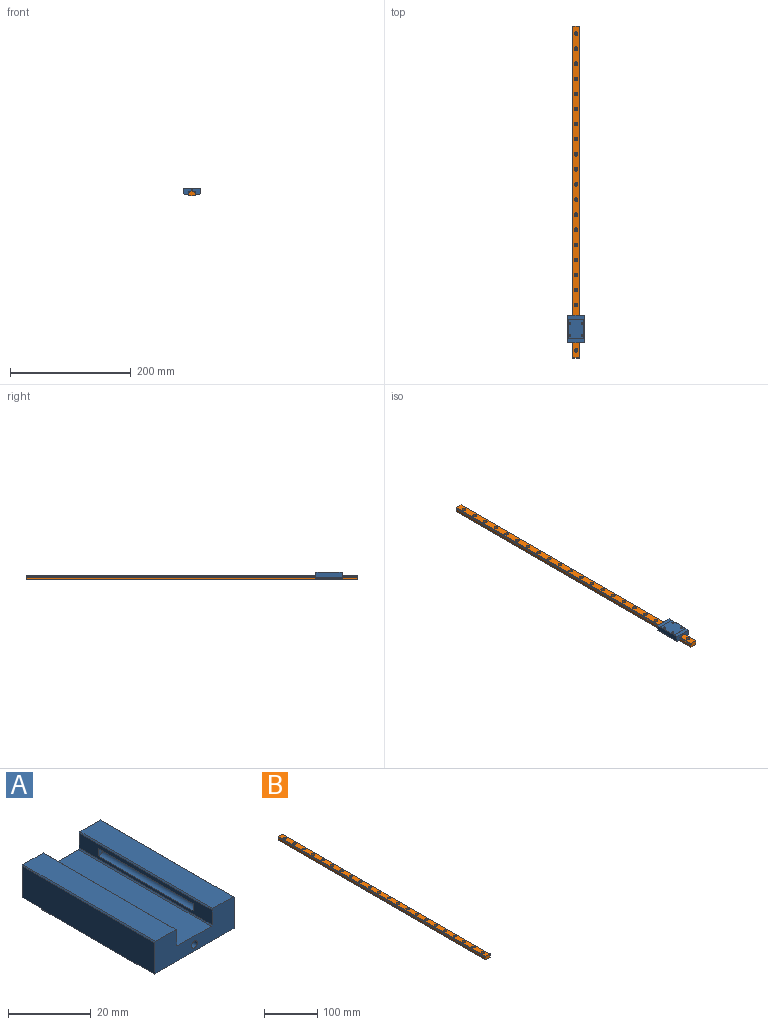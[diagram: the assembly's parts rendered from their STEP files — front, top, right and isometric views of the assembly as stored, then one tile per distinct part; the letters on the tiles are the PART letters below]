
ASSEMBLY  parts=2 mates=1
PART A: 37 faces, bbox 27x45.4x10 mm
  f0: plane 45.4x0.3mm, normal (-0.71,0,0.71), area 19.3mm2, adj f3,f6,f22,f23
  f1: plane 45.4x0.3mm, normal (0.71,0,0.71), area 19.3mm2, adj f10,f11,f22,f23
  f2: plane 45.4x0.3mm, normal (0.71,0,0.71), area 19.3mm2, adj f6,f7,f22,f23
  f3: plane 45.4x4.4mm, normal (-1,0,0), area 129.2mm2, adj f0,f5,f17,f20,f22,f23,f24
  f4: plane 45.4x11.4mm, normal (0,0,1), area 517.6mm2, adj f16,f17,f22,f23
  f5: cylinder r=1.15mm len=32.4mm, axis (0,-1,0), area 141.5mm2, adj f3,f20,f24
  f6: plane 45.4x6.9mm, normal (0,0,1), area 313.3mm2, adj f0,f2,f22,f23
  f7: plane 45.4x9.4mm, normal (1,0,0), area 424.2mm2, adj f2,f15,f18,f21,f22,f23,f25,f35
  f8: plane 32.4x26.4mm, normal (0,0,-1), area 821.1mm2, adj f14,f15,f18,f27,f29,f31,f33,f35
  f9: plane 45.4x9.4mm, normal (-1,0,0), area 424.2mm2, adj f14,f18,f21,f22,f23,f25,f34,f35
  f10: plane 45.4x6.9mm, normal (0,0,1), area 313.3mm2, adj f1,f22,f23,f34
  f11: plane 45.4x4.4mm, normal (1,0,0), area 129.2mm2, adj f1,f12,f16,f19,f22,f23,f36
  f12: cylinder r=1.15mm len=32.4mm, axis (0,-1,0), area 141.5mm2, adj f11,f19,f36
  f13: cylinder r=1mm len=45.4mm, axis (0,-1,0), area 285.3mm2, adj f22,f23
  f14: plane 32.4x0.3mm, normal (-0.71,0,-0.71), area 13.7mm2, adj f8,f9,f18,f35
  f15: plane 32.4x0.3mm, normal (0.71,0,-0.71), area 13.7mm2, adj f7,f8,f18,f35
  f16: plane 45.4x0.3mm, normal (0.71,0,0.71), area 19.3mm2, adj f4,f11,f22,f23
  f17: plane 45.4x0.3mm, normal (-0.71,0,0.71), area 19.3mm2, adj f3,f4,f22,f23
  f18: plane 27x0.5mm, normal (0,-1,0), area 13.4mm2, adj f7,f8,f9,f14,f15,f21
  f19: plane 2.3x1.52mm, normal (0,1,0), area 2.9mm2, adj f11,f12
  f20: plane 2.3x1.52mm, normal (0,1,0), area 2.9mm2, adj f3,f5
  f21: plane 27x6.5mm, normal (0,0,-1), area 175.5mm2, adj f7,f9,f18,f22
  f22: plane 27x9.5mm, normal (0,-1,0), area 193.3mm2, adj f0,f1,f2,f3,f4,f6,f7,f9
  f23: plane 27x9.5mm, normal (0,1,0), area 193.3mm2, adj f0,f1,f2,f3,f4,f6,f7,f9
  f24: plane 2.3x1.52mm, normal (0,-1,0), area 2.9mm2, adj f3,f5
  f25: plane 27x6.5mm, normal (0,0,-1), area 175.5mm2, adj f7,f9,f23,f35
  f26: cone r=857.17mm half-angle=59deg, axis (0,0,-1), area 10mm2, adj f27
  f27: cylinder r=1.65mm len=3.5mm, axis (0,0,1), area 36.3mm2, adj f8,f26
  f28: cone r=857.17mm half-angle=59deg, axis (0,0,-1), area 10mm2, adj f29
  f29: cylinder r=1.65mm len=3.5mm, axis (0,0,1), area 36.3mm2, adj f8,f28
  f30: cone r=857.17mm half-angle=59deg, axis (0,0,-1), area 10mm2, adj f31
  f31: cylinder r=1.65mm len=3.5mm, axis (0,0,1), area 36.3mm2, adj f8,f30
  f32: cone r=857.17mm half-angle=59deg, axis (0,0,-1), area 10mm2, adj f33
  f33: cylinder r=1.65mm len=3.5mm, axis (0,0,1), area 36.3mm2, adj f8,f32
  f34: plane 45.4x0.3mm, normal (-0.71,0,0.71), area 19.3mm2, adj f9,f10,f22,f23
  f35: plane 27x0.5mm, normal (0,1,0), area 13.4mm2, adj f7,f8,f9,f14,f15,f25
  f36: plane 2.3x1.52mm, normal (0,-1,0), area 2.9mm2, adj f11,f12
PART B: 88 faces, bbox 12x550x8 mm
  f0: plane 550x0.51mm, normal (0,0,1), area 280.4mm2, adj f1,f19,f20,f84
  f1: plane 550x0.3mm, normal (1,0,0), area 165mm2, adj f0,f2,f20,f84
  f2: plane 550x0.51mm, normal (0,0,-1), area 280.4mm2, adj f1,f3,f20,f84
  f3: cylinder r=1.15mm len=550mm, axis (0,1,0), area 703.6mm2, adj f2,f4,f20,f84
  f4: plane 550x0.86mm, normal (1,0,0), area 473.5mm2, adj f3,f5,f20,f84
  f5: plane 550x0.35mm, normal (0.71,0,0.71), area 272.2mm2, adj f4,f6,f20,f84
  f6: plane 550x11.3mm, normal (0,0,1), area 5593mm2, adj f5,f7,f20,f23,f26,f29,f32,f35
  f7: plane 550x0.35mm, normal (-0.71,0,0.71), area 272.2mm2, adj f6,f8,f20,f84
  f8: plane 550x0.86mm, normal (-1,0,0), area 473.5mm2, adj f7,f9,f20,f84
  f9: cylinder r=1.15mm len=550mm, axis (0,1,0), area 703.6mm2, adj f8,f10,f20,f84
  f10: plane 550x0.51mm, normal (0,0,-1), area 280.4mm2, adj f9,f11,f20,f84
  f11: plane 550x0.3mm, normal (-1,0,0), area 165mm2, adj f10,f12,f20,f84
  f12: plane 550x0.51mm, normal (0,0,1), area 280.4mm2, adj f11,f13,f20,f84
  f13: cylinder r=1.15mm len=550mm, axis (0,1,0), area 703.6mm2, adj f12,f14,f20,f84
  f14: plane 550x4.26mm, normal (-1,0,0), area 2343.7mm2, adj f13,f15,f20,f84
  f15: plane 550x0.35mm, normal (-0.71,0,-0.71), area 272.2mm2, adj f14,f16,f20,f84
  f16: plane 550x11.3mm, normal (0,0,-1), area 6003.3mm2, adj f15,f17,f20,f21,f24,f27,f30,f33
  f17: plane 550x0.35mm, normal (0.71,0,-0.71), area 272.2mm2, adj f16,f18,f20,f84
  f18: plane 550x4.26mm, normal (1,0,0), area 2343.7mm2, adj f17,f19,f20,f84
  f19: cylinder r=1.15mm len=550mm, axis (0,1,0), area 703.6mm2, adj f0,f18,f20,f84
  f20: plane 12x8mm, normal (0,-1,0), area 93mm2, adj f0,f1,f2,f3,f4,f5,f6,f7
  f21: cylinder r=1.75mm len=3.5mm, axis (0,0,1), area 38.5mm2, adj f16,f22
  f22: plane 6x6mm, normal (0,0,1), area 18.7mm2, adj f21,f23
  f23: cylinder r=3mm len=6mm, axis (0,0,1), area 84.8mm2, adj f6,f22
  f24: cylinder r=1.75mm len=3.5mm, axis (0,0,1), area 38.5mm2, adj f16,f25
  f25: plane 6x6mm, normal (0,0,1), area 18.7mm2, adj f24,f26
  f26: cylinder r=3mm len=6mm, axis (0,0,1), area 84.8mm2, adj f6,f25
  f27: cylinder r=1.75mm len=3.5mm, axis (0,0,1), area 38.5mm2, adj f16,f28
  f28: plane 6x6mm, normal (0,0,1), area 18.7mm2, adj f27,f29
  f29: cylinder r=3mm len=6mm, axis (0,0,1), area 84.8mm2, adj f6,f28
  f30: cylinder r=1.75mm len=3.5mm, axis (0,0,1), area 38.5mm2, adj f16,f31
  f31: plane 6x6mm, normal (0,0,1), area 18.7mm2, adj f30,f32
  f32: cylinder r=3mm len=6mm, axis (0,0,1), area 84.8mm2, adj f6,f31
  f33: cylinder r=1.75mm len=3.5mm, axis (0,0,1), area 38.5mm2, adj f16,f34
  f34: plane 6x6mm, normal (0,0,1), area 18.7mm2, adj f33,f35
  f35: cylinder r=3mm len=6mm, axis (0,0,1), area 84.8mm2, adj f6,f34
  f36: cylinder r=1.75mm len=3.5mm, axis (0,0,1), area 38.5mm2, adj f16,f37
  f37: plane 6x6mm, normal (0,0,1), area 18.7mm2, adj f36,f38
  f38: cylinder r=3mm len=6mm, axis (0,0,1), area 84.8mm2, adj f6,f37
  f39: cylinder r=1.75mm len=3.5mm, axis (0,0,1), area 38.5mm2, adj f16,f40
  f40: plane 6x6mm, normal (0,0,1), area 18.7mm2, adj f39,f41
  f41: cylinder r=3mm len=6mm, axis (0,0,1), area 84.8mm2, adj f6,f40
  f42: cylinder r=1.75mm len=3.5mm, axis (0,0,1), area 38.5mm2, adj f16,f43
  f43: plane 6x6mm, normal (0,0,1), area 18.7mm2, adj f42,f44
  f44: cylinder r=3mm len=6mm, axis (0,0,1), area 84.8mm2, adj f6,f43
  f45: cylinder r=1.75mm len=3.5mm, axis (0,0,1), area 38.5mm2, adj f16,f46
  f46: plane 6x6mm, normal (0,0,1), area 18.7mm2, adj f45,f47
  f47: cylinder r=3mm len=6mm, axis (0,0,1), area 84.8mm2, adj f6,f46
  f48: cylinder r=1.75mm len=3.5mm, axis (0,0,1), area 38.5mm2, adj f16,f49
  f49: plane 6x6mm, normal (0,0,1), area 18.7mm2, adj f48,f50
  f50: cylinder r=3mm len=6mm, axis (0,0,1), area 84.8mm2, adj f6,f49
  f51: cylinder r=1.75mm len=3.5mm, axis (0,0,1), area 38.5mm2, adj f16,f52
  f52: plane 6x6mm, normal (0,0,1), area 18.7mm2, adj f51,f53
  f53: cylinder r=3mm len=6mm, axis (0,0,1), area 84.8mm2, adj f6,f52
  f54: cylinder r=1.75mm len=3.5mm, axis (0,0,1), area 38.5mm2, adj f16,f55
  f55: plane 6x6mm, normal (0,0,1), area 18.7mm2, adj f54,f56
  f56: cylinder r=3mm len=6mm, axis (0,0,1), area 84.8mm2, adj f6,f55
  f57: cylinder r=1.75mm len=3.5mm, axis (0,0,1), area 38.5mm2, adj f16,f58
  f58: plane 6x6mm, normal (0,0,1), area 18.7mm2, adj f57,f59
  f59: cylinder r=3mm len=6mm, axis (0,0,1), area 84.8mm2, adj f6,f58
  f60: cylinder r=1.75mm len=3.5mm, axis (0,0,1), area 38.5mm2, adj f16,f61
  f61: plane 6x6mm, normal (0,0,1), area 18.7mm2, adj f60,f62
  f62: cylinder r=3mm len=6mm, axis (0,0,1), area 84.8mm2, adj f6,f61
  f63: cylinder r=1.75mm len=3.5mm, axis (0,0,1), area 38.5mm2, adj f16,f64
  f64: plane 6x6mm, normal (0,0,1), area 18.7mm2, adj f63,f65
  f65: cylinder r=3mm len=6mm, axis (0,0,1), area 84.8mm2, adj f6,f64
  f66: cylinder r=1.75mm len=3.5mm, axis (0,0,1), area 38.5mm2, adj f16,f67
  f67: plane 6x6mm, normal (0,0,1), area 18.7mm2, adj f66,f68
  f68: cylinder r=3mm len=6mm, axis (0,0,1), area 84.8mm2, adj f6,f67
  f69: cylinder r=1.75mm len=3.5mm, axis (0,0,1), area 38.5mm2, adj f16,f70
  f70: plane 6x6mm, normal (0,0,1), area 18.7mm2, adj f69,f71
  f71: cylinder r=3mm len=6mm, axis (0,0,1), area 84.8mm2, adj f6,f70
  f72: cylinder r=1.75mm len=3.5mm, axis (0,0,1), area 38.5mm2, adj f16,f73
  f73: plane 6x6mm, normal (0,0,1), area 18.7mm2, adj f72,f74
  f74: cylinder r=3mm len=6mm, axis (0,0,1), area 84.8mm2, adj f6,f73
  f75: cylinder r=1.75mm len=3.5mm, axis (0,0,1), area 38.5mm2, adj f16,f76
  f76: plane 6x6mm, normal (0,0,1), area 18.7mm2, adj f75,f77
  f77: cylinder r=3mm len=6mm, axis (0,0,1), area 84.8mm2, adj f6,f76
  f78: cylinder r=1.75mm len=3.5mm, axis (0,0,1), area 38.5mm2, adj f16,f79
  f79: plane 6x6mm, normal (0,0,1), area 18.7mm2, adj f78,f80
  f80: cylinder r=3mm len=6mm, axis (0,0,1), area 84.8mm2, adj f6,f79
  f81: cylinder r=1.75mm len=3.5mm, axis (0,0,1), area 38.5mm2, adj f16,f82
  f82: plane 6x6mm, normal (0,0,1), area 18.7mm2, adj f81,f83
  f83: cylinder r=3mm len=6mm, axis (0,0,1), area 84.8mm2, adj f6,f82
  f84: plane 12x8mm, normal (0,1,0), area 93mm2, adj f0,f1,f2,f3,f4,f5,f6,f7
  f85: cylinder r=1.75mm len=3.5mm, axis (0,0,1), area 38.5mm2, adj f16,f86
  f86: plane 6x6mm, normal (0,0,1), area 18.7mm2, adj f85,f87
  f87: cylinder r=3mm len=6mm, axis (0,0,1), area 84.8mm2, adj f6,f86
PLACE A rot(axis=(0,1,0),180deg) t=(-12.45,82.04,13.68)mm
PLACE B t=(-12.45,43,13.68)mm fixed
MATE slider B.f20 <-> A.f22  axis (0,-1,0) through (-12.45,18,13.68)mm
